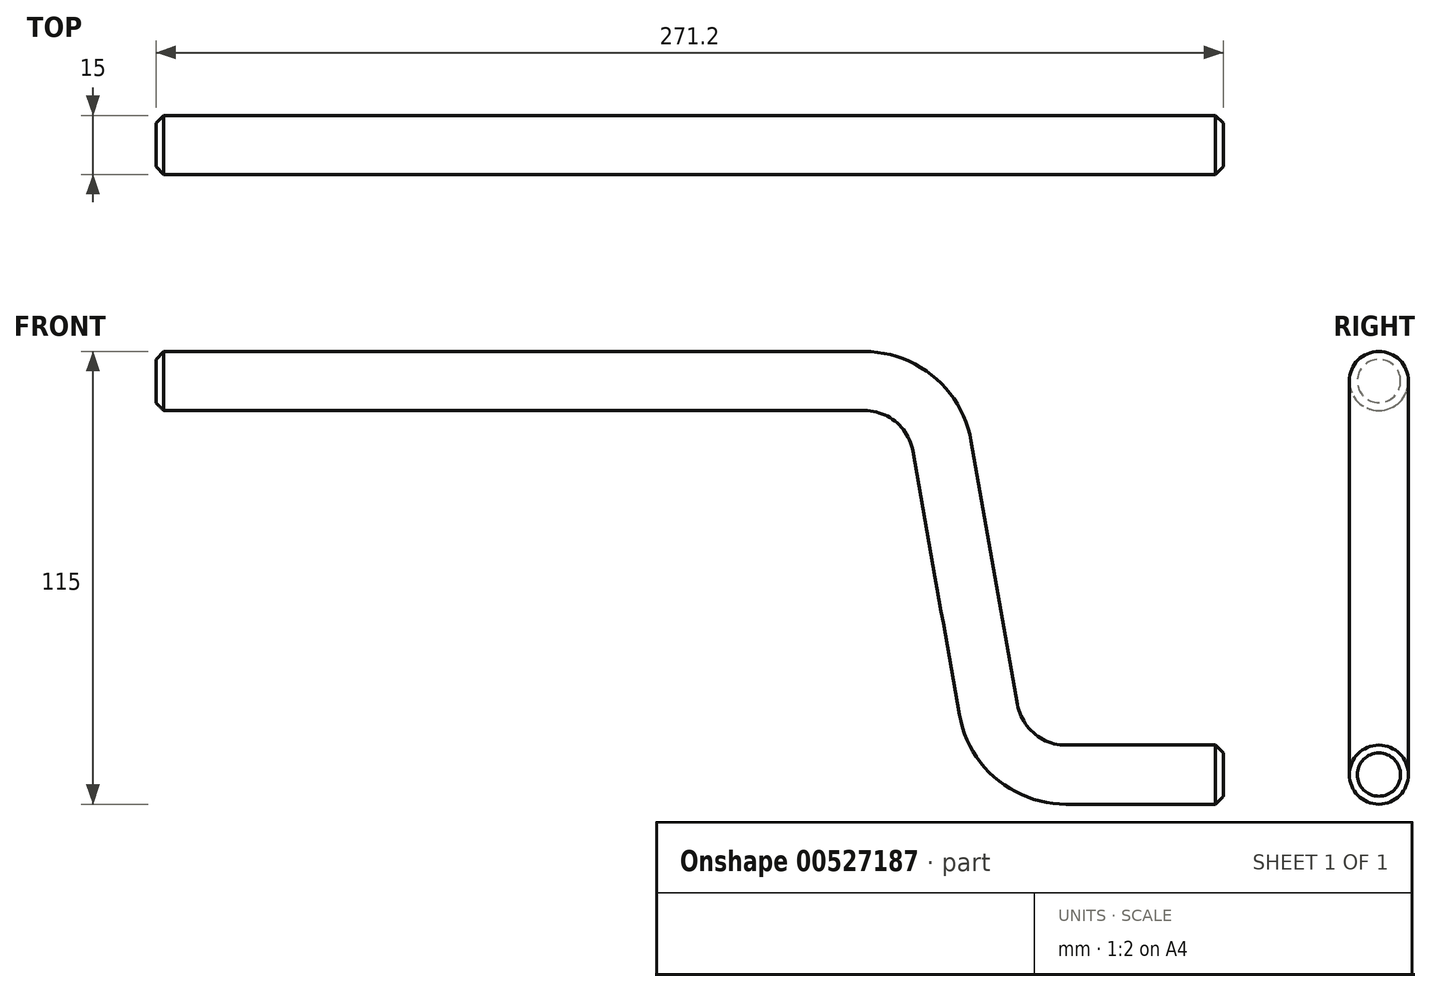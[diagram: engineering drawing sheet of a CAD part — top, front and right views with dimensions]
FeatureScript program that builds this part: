
annotation { "Feature Type Name" : "Feature", "Feature Type Description" : "" }
export const myFeature = defineFeature(function(context is Context, id is Id, definition is map)
    precondition{}
    {
        {
            var Q0;
            Q0=qCreatedBy(makeId("Front.planeOp"),FACE);
            var sketch = newSketch(context, id + "F0", { "sketchPlane" : qUnion([Q0])});
            skLineSegment(sketch, "E0", {"start": v(-89.5, 0) * mm, "end": v(90.5, 0) * mm});
            skLineSegment(sketch, "E1", {"start": v(110.2, -16.53) * mm, "end": v(122, -83.47) * mm});
            skLineSegment(sketch, "E2", {"start": v(141.7, -100) * mm, "end": v(181.7, -100) * mm});
            skPoint(sketch, "E3.visualSharp", {"position": v(107.28, 0) * mm});
            skArc(sketch, "E3.filletArc", {"start": v(110.2, -16.53) * mm, "mid": v(103.36, -4.68) * mm, "end": v(90.5, 0) * mm});
            skPoint(sketch, "E4.visualSharp", {"position": v(124.91, -100) * mm});
            skArc(sketch, "E4.filletArc", {"start": v(122, -83.47) * mm, "mid": v(128.84, -95.32) * mm, "end": v(141.7, -100) * mm});
            skSolve(sketch);
        }
        {
            var Q0;
            Q0=qCreatedBy(makeId("Right.planeOp"),FACE);
            cPlane(context, id + "F1", {"entities" : qUnion([Q0]), "cplaneType" : CPlaneType.OFFSET, "offset" : 89.5 * mm, "oppositeDirection" : true, "width" : 150 * mm, "height" : 150 * mm});
        }
        {
            var Q0;
            Q0=qCreatedBy(id+"F1.planeOp",FACE);
            var sketch = newSketch(context, id + "F2", { "sketchPlane" : qUnion([Q0])});
            skCircle(sketch, "E5", {"center": v(0, 0) * mm, "radius": 7.5 * mm});
            skSolve(sketch);
        }
        {
            var Q0;
            Q0=makeQuery(id+"F2.imprint","IMPRINT",FACE,{"disambiguationData":[TD([[makeQuery(id+"F2.imprint","IMPRINT",EDGE,{"derivedFrom":sQuery(id+"F2.wireOp",EDGE,"E5")}),1.0]])]});
            var Q1;
            Q1=sQuery(id+"F0.wireOp",EDGE,"E0");
            var Q2;
            Q2=sQuery(id+"F0.wireOp",EDGE,"E3.filletArc");
            var Q3;
            Q3=sQuery(id+"F0.wireOp",EDGE,"E1");
            var Q4;
            Q4=sQuery(id+"F0.wireOp",EDGE,"E4.filletArc");
            var Q5;
            Q5=sQuery(id+"F0.wireOp",EDGE,"E2");
            sweep(context, id + "F3", {"profiles" : qUnion([Q0]), "path" : qUnion([Q1, Q2, Q3, Q4, Q5])});
        }
        {
            var Q0;
            Q0=makeQuery(id+"F3.opSweep","CAP_EDGE",EDGE,{"disambiguationData":[OSD([sQuery(id+"F0.wireOp",VERTEX,"E2.end"),sQuery(id+"F2.wireOp",EDGE,"E5")])],"isStart":false});
            var Q1;
            Q1=makeQuery(id+"F3.opSweep","CAP_EDGE",EDGE,{"disambiguationData":[OSD([sQuery(id+"F0.wireOp",VERTEX,"E0.start"),sQuery(id+"F2.wireOp",EDGE,"E5")])],"isStart":true});
            chamfer(context, id + "F4", {"entities" : qUnion([Q0, Q1]), "width" : 2 * mm, "tangentPropagation" : true});
        }
    });
